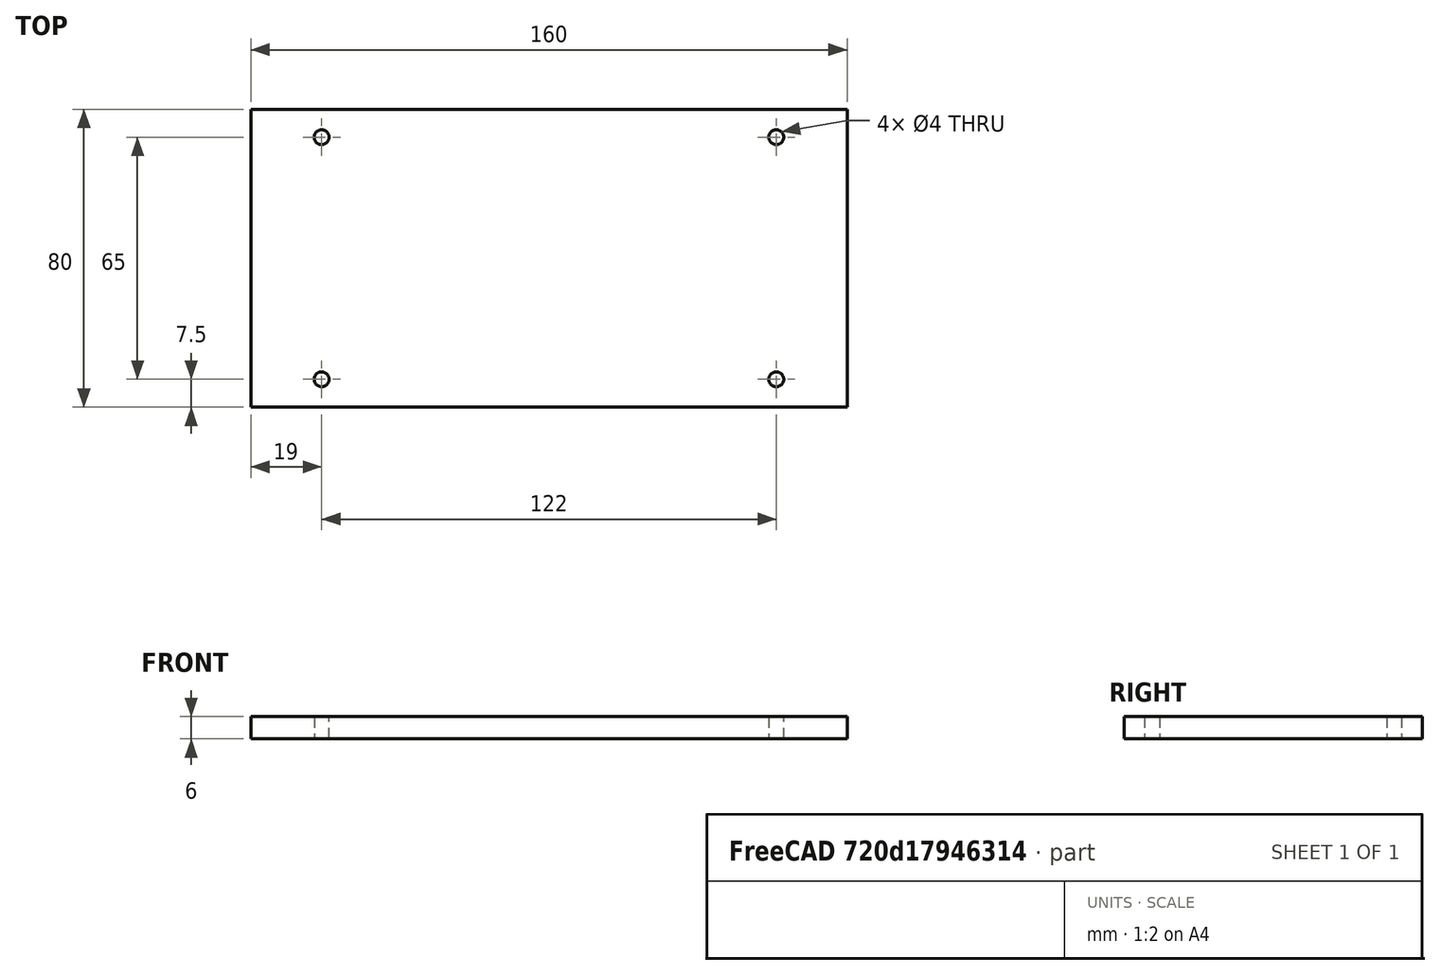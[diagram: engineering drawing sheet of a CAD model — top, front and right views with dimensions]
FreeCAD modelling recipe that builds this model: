
FCSTD DOCUMENT  (FreeCAD 0.18R4 (GitTag))
Label: LiDAR_Mounting_Plate
License: All rights reserved
LicenseURL: http://en.wikipedia.org/wiki/All_rights_reserved
objects: Sketcher::SketchObject×1, PartDesign::Pad×1, PartDesign::Body×1
note: 4 computed .brp shape members not serialized (recipe doc carries the construction recipe); baked Part::Feature solids carry a one-line shape summary decoded from their .brp

FEATURE [Sketcher::SketchObject] Sketch
  MapMode = 5
  Support = -> [XY_Plane]
  sketch-geometry (8):
    g0: LineSegment StartX=-80 StartY=40 StartZ=0 EndX=80 EndY=40 EndZ=0
    g1: LineSegment StartX=80 StartY=40 StartZ=0 EndX=80 EndY=-40 EndZ=0
    g2: LineSegment StartX=80 StartY=-40 StartZ=0 EndX=-80 EndY=-40 EndZ=0
    g3: LineSegment StartX=-80 StartY=-40 StartZ=0 EndX=-80 EndY=40 EndZ=0
    g4: Circle CenterX=-61 CenterY=32.5 CenterZ=0 NormalX=0 NormalY=0 NormalZ=1 AngleXU=0 Radius=2
    g5: Circle CenterX=-61 CenterY=-32.5 CenterZ=0 NormalX=0 NormalY=0 NormalZ=1 AngleXU=0 Radius=2
    g6: Circle CenterX=61 CenterY=32.5 CenterZ=0 NormalX=0 NormalY=0 NormalZ=1 AngleXU=0 Radius=2
    g7: Circle CenterX=61 CenterY=-32.5 CenterZ=0 NormalX=0 NormalY=0 NormalZ=1 AngleXU=0 Radius=2
  constraints (22):
    c: Coincident(g0,g1)
    c: Coincident(g1,g2)
    c: Coincident(g2,g3)
    c: Coincident(g3,g0)
    c: Horizontal(g2)
    c: Vertical(g3)
    c: Symmetric(g0,g1,g-1)
    c: Symmetric(g0,g0,g-2)
    c: DistanceX(g0,g0) = 160
    c: DistanceY(g1,g1) = 80
    c: Radius(g4) = 2
    c: Distance(g4,g-2) = 61
    c: Distance(g4,g-1) = 32.5
    c: Radius(g5) = 2
    c: Distance(g5,g-1) = 32.5
    c: Distance(g5,g-2) = 61
    c: Radius(g6) = 2
    c: Distance(g6,g-2) = 61
    c: Distance(g6,g-1) = 32.5
    c: Radius(g7) = 2
    c: Distance(g7,g-1) = 32.5
    c: Distance(g7,g-2) = 61
FEATURE [PartDesign::Pad] Pad
  Length = 6
  Length2 = 100
  Profile = -> Sketch
  Type = 0
FEATURE [PartDesign::Body] Body
  Group = -> [Sketch,Pad]
  Origin = -> Origin
  Tip = -> Pad
